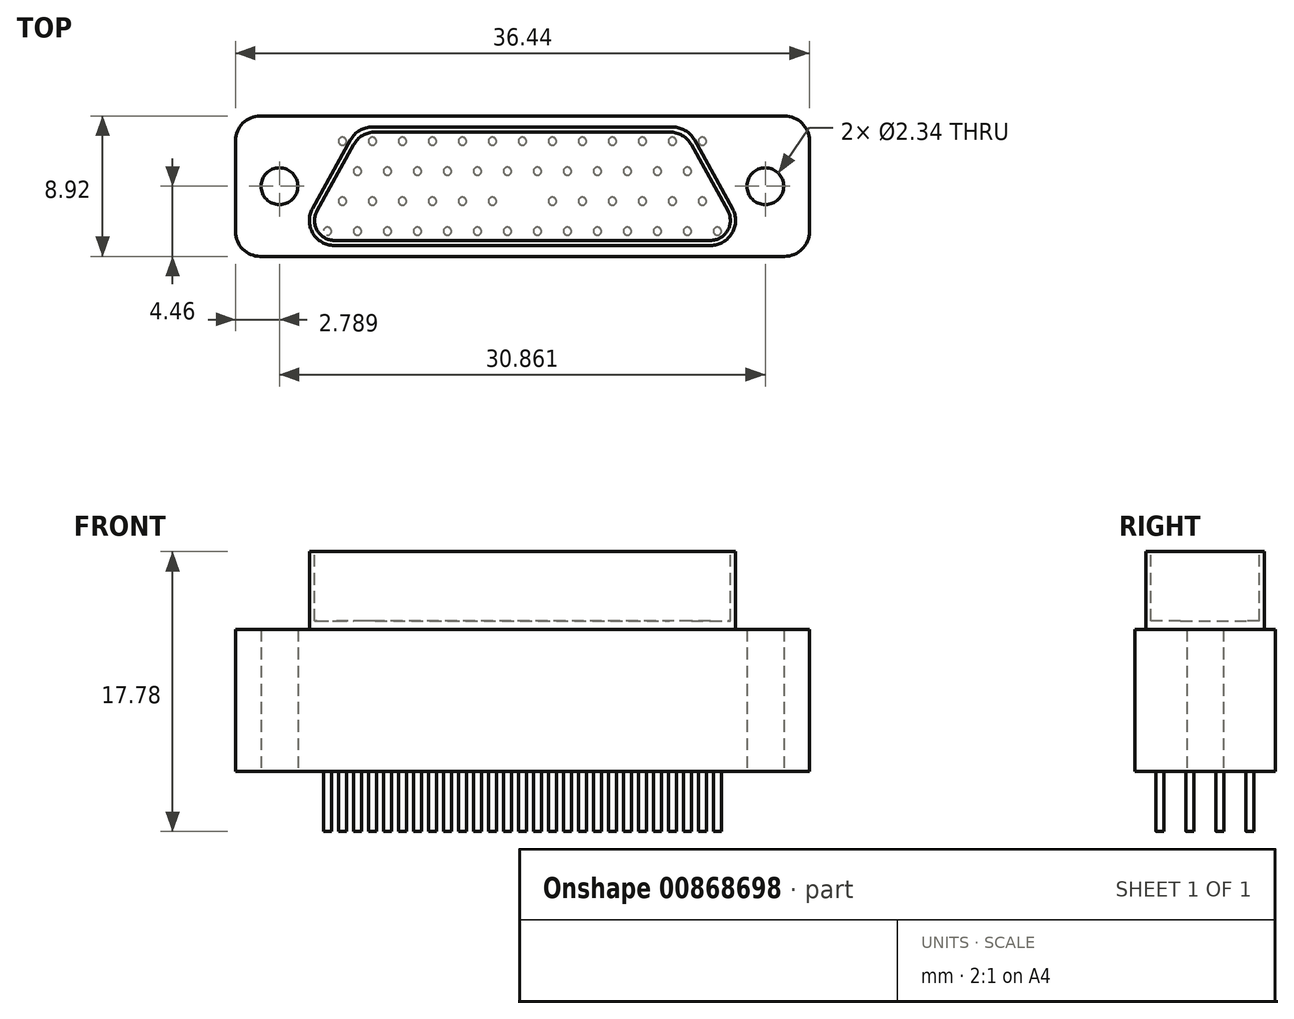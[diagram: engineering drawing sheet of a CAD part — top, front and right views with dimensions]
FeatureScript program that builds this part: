
annotation { "Feature Type Name" : "Feature", "Feature Type Description" : "" }
export const myFeature = defineFeature(function(context is Context, id is Id, definition is map)
    precondition{}
    {
        {
            var Q0;
            Q0=qCreatedBy(makeId("Top.planeOp"),FACE);
            var sketch = newSketch(context, id + "F0", { "sketchPlane" : qUnion([Q0])});
            skLineSegment(sketch, "E0.bottom", {"start": v(-16.65, 4.46) * mm, "end": v(16.65, 4.46) * mm});
            skLineSegment(sketch, "E0.top", {"start": v(-16.65, -4.46) * mm, "end": v(16.65, -4.46) * mm});
            skLineSegment(sketch, "E0.left", {"start": v(-18.22, 2.88) * mm, "end": v(-18.22, -2.88) * mm});
            skLineSegment(sketch, "E0.right", {"start": v(18.22, 2.88) * mm, "end": v(18.22, -2.88) * mm});
            skPoint(sketch, "E0.middle", {"position": v(0, 0) * mm});
            skCircle(sketch, "E1", {"center": v(-15.43, 0) * mm, "radius": 1.17 * mm});
            skCircle(sketch, "E2", {"center": v(15.43, 0) * mm, "radius": 1.17 * mm});
            skPoint(sketch, "E3.visualSharp", {"position": v(-18.22, -4.46) * mm});
            skArc(sketch, "E3.filletArc", {"start": v(-18.22, -2.88) * mm, "mid": v(-17.76, -4) * mm, "end": v(-16.65, -4.46) * mm});
            skPoint(sketch, "E4.visualSharp", {"position": v(-18.22, 4.46) * mm});
            skArc(sketch, "E4.filletArc", {"start": v(-16.65, 4.46) * mm, "mid": v(-17.76, 4) * mm, "end": v(-18.22, 2.88) * mm});
            skPoint(sketch, "E5.visualSharp", {"position": v(18.22, 4.46) * mm});
            skArc(sketch, "E5.filletArc", {"start": v(18.22, 2.88) * mm, "mid": v(17.76, 4) * mm, "end": v(16.65, 4.46) * mm});
            skPoint(sketch, "E6.visualSharp", {"position": v(18.22, -4.46) * mm});
            skArc(sketch, "E6.filletArc", {"start": v(16.65, -4.46) * mm, "mid": v(17.76, -4) * mm, "end": v(18.22, -2.88) * mm});
            skSolve(sketch);
        }
        {
            var Q0;
            Q0=makeQuery(id+"F0.imprint","IMPRINT",FACE,{"disambiguationData":[TD([[makeQuery(id+"F0.imprint","IMPRINT",EDGE,{"derivedFrom":sQuery(id+"F0.wireOp",EDGE,"E0.bottom")}),-1.0]])]});
            extrude(context, id + "F1", {"entities" : qUnion([Q0]), "endBound" : BoundingType.SYMMETRIC, "depth" : 9.02 * mm, "offsetDistance" : 25.4 * mm});
        }
        {
            var Q0;
            Q0=makeQuery(id+"F1.opExtrude","CAP_FACE",FACE,{"disambiguationData":[OSD([sQuery(id+"F0.wireOp",EDGE,"E0.bottom"),sQuery(id+"F0.wireOp",EDGE,"E0.top"),sQuery(id+"F0.wireOp",EDGE,"E0.left"),sQuery(id+"F0.wireOp",EDGE,"E0.right"),sQuery(id+"F0.wireOp",EDGE,"E1"),sQuery(id+"F0.wireOp",EDGE,"E2"),sQuery(id+"F0.wireOp",EDGE,"E3.filletArc"),sQuery(id+"F0.wireOp",EDGE,"E4.filletArc"),sQuery(id+"F0.wireOp",EDGE,"E5.filletArc"),sQuery(id+"F0.wireOp",EDGE,"E6.filletArc")])],"isStart":false});
            var sketch = newSketch(context, id + "F2", { "sketchPlane" : qUnion([Q0])});
            skPoint(sketch, "E7.middle", {"position": v(0, 0) * mm});
            skLineSegment(sketch, "E8.top", {"start": v(11.96, -3.76) * mm, "end": v(-11.96, -3.76) * mm});
            skLineSegment(sketch, "E9", {"start": v(-9.54, 3.76) * mm, "end": v(9.54, 3.76) * mm});
            skLineSegment(sketch, "E10", {"start": v(-13.33, -1.42) * mm, "end": v(-10.91, 2.95) * mm});
            skLineSegment(sketch, "E11", {"start": v(10.91, 2.95) * mm, "end": v(13.34, -1.42) * mm});
            skPoint(sketch, "E12.visualSharp", {"position": v(-10.46, 3.76) * mm});
            skArc(sketch, "E12.filletArc", {"start": v(-9.54, 3.76) * mm, "mid": v(-10.33, 3.54) * mm, "end": v(-10.91, 2.95) * mm});
            skPoint(sketch, "E13.visualSharp", {"position": v(-14.63, -3.76) * mm});
            skArc(sketch, "E13.filletArc", {"start": v(-13.33, -1.42) * mm, "mid": v(-13.31, -2.98) * mm, "end": v(-11.96, -3.76) * mm});
            skPoint(sketch, "E14.visualSharp", {"position": v(14.63, -3.76) * mm});
            skArc(sketch, "E14.filletArc", {"start": v(11.96, -3.76) * mm, "mid": v(13.32, -2.98) * mm, "end": v(13.34, -1.42) * mm});
            skPoint(sketch, "E15.visualSharp", {"position": v(10.46, 3.76) * mm});
            skArc(sketch, "E15.filletArc", {"start": v(10.91, 2.95) * mm, "mid": v(10.34, 3.54) * mm, "end": v(9.54, 3.76) * mm});
            skSolve(sketch);
        }
        {
            var Q0;
            Q0=qSketchRegion(id+"F2",true);
            extrude(context, id + "F3", {"entities" : qUnion([Q0]), "operationType" : NewBodyOperationType.ADD, "depth" : 4.95 * mm, "offsetDistance" : 25.4 * mm});
        }
        {
            var Q0;
            Q0=makeQuery(id+"F3.opExtrude","CAP_FACE",FACE,{"disambiguationData":[OSD([sQuery(id+"F2.wireOp",EDGE,"E8.top"),sQuery(id+"F2.wireOp",EDGE,"E9"),sQuery(id+"F2.wireOp",EDGE,"E10"),sQuery(id+"F2.wireOp",EDGE,"E11"),sQuery(id+"F2.wireOp",EDGE,"E12.filletArc"),sQuery(id+"F2.wireOp",EDGE,"E13.filletArc"),sQuery(id+"F2.wireOp",EDGE,"E14.filletArc"),sQuery(id+"F2.wireOp",EDGE,"E15.filletArc")])],"isStart":false});
            var sketch = newSketch(context, id + "F4", { "sketchPlane" : qUnion([Q0])});
            skLineSegment(sketch, "E16", {"start": v(-9.35, 3.44) * mm, "end": v(9.35, 3.44) * mm});
            skLineSegment(sketch, "E17", {"start": v(10.73, 2.63) * mm, "end": v(13.05, -1.56) * mm});
            skLineSegment(sketch, "E18", {"start": v(11.94, -3.44) * mm, "end": v(-11.94, -3.44) * mm});
            skLineSegment(sketch, "E19", {"start": v(-13.05, -1.56) * mm, "end": v(-10.73, 2.63) * mm});
            skPoint(sketch, "E20.visualSharp", {"position": v(-14.1, -3.44) * mm});
            skArc(sketch, "E20.filletArc", {"start": v(-13.05, -1.56) * mm, "mid": v(-13.03, -2.82) * mm, "end": v(-11.94, -3.44) * mm});
            skPoint(sketch, "E21.visualSharp", {"position": v(-10.28, 3.44) * mm});
            skArc(sketch, "E21.filletArc", {"start": v(-9.35, 3.44) * mm, "mid": v(-10.15, 3.22) * mm, "end": v(-10.73, 2.63) * mm});
            skPoint(sketch, "E22.visualSharp", {"position": v(10.28, 3.44) * mm});
            skArc(sketch, "E22.filletArc", {"start": v(10.73, 2.63) * mm, "mid": v(10.15, 3.22) * mm, "end": v(9.35, 3.44) * mm});
            skPoint(sketch, "E23.visualSharp", {"position": v(14.1, -3.44) * mm});
            skArc(sketch, "E23.filletArc", {"start": v(11.94, -3.44) * mm, "mid": v(13.03, -2.82) * mm, "end": v(13.05, -1.56) * mm});
            skSolve(sketch);
        }
        {
            var Q0;
            Q0=qSketchRegion(id+"F4",true);
            extrude(context, id + "F5", {"entities" : qUnion([Q0]), "operationType" : NewBodyOperationType.REMOVE, "depth" : -4.4 * mm, "offsetDistance" : 25.4 * mm});
        }
        {
            var Q0;
            Q0=makeQuery(id+"F1.opExtrude","CAP_FACE",FACE,{"disambiguationData":[OSD([sQuery(id+"F0.wireOp",EDGE,"E0.bottom"),sQuery(id+"F0.wireOp",EDGE,"E0.top"),sQuery(id+"F0.wireOp",EDGE,"E0.left"),sQuery(id+"F0.wireOp",EDGE,"E0.right"),sQuery(id+"F0.wireOp",EDGE,"E1"),sQuery(id+"F0.wireOp",EDGE,"E2"),sQuery(id+"F0.wireOp",EDGE,"E3.filletArc"),sQuery(id+"F0.wireOp",EDGE,"E4.filletArc"),sQuery(id+"F0.wireOp",EDGE,"E5.filletArc"),sQuery(id+"F0.wireOp",EDGE,"E6.filletArc")])],"isStart":true});
            var sketch = newSketch(context, id + "F6", { "sketchPlane" : qUnion([Q0])});
            skCircle(sketch, "E24", {"center": v(-12.38, 2.86) * mm, "radius": 0.25 * mm});
            skCircle(sketch, "E25.1.0.0", {"center": v(-10.48, 2.86) * mm, "radius": 0.25 * mm});
            skCircle(sketch, "E25.2.0.0", {"center": v(-8.57, 2.86) * mm, "radius": 0.25 * mm});
            skCircle(sketch, "E25.3.0.0", {"center": v(-6.67, 2.86) * mm, "radius": 0.25 * mm});
            skCircle(sketch, "E25.4.0.0", {"center": v(-4.76, 2.86) * mm, "radius": 0.25 * mm});
            skCircle(sketch, "E25.5.0.0", {"center": v(-2.86, 2.86) * mm, "radius": 0.25 * mm});
            skCircle(sketch, "E25.6.0.0", {"center": v(-0.95, 2.86) * mm, "radius": 0.25 * mm});
            skCircle(sketch, "E25.7.0.0", {"center": v(0.95, 2.86) * mm, "radius": 0.25 * mm});
            skCircle(sketch, "E25.8.0.0", {"center": v(2.86, 2.86) * mm, "radius": 0.25 * mm});
            skCircle(sketch, "E25.9.0.0", {"center": v(4.76, 2.86) * mm, "radius": 0.25 * mm});
            skCircle(sketch, "E25.10.0.0", {"center": v(6.67, 2.86) * mm, "radius": 0.25 * mm});
            skCircle(sketch, "E25.11.0.0", {"center": v(8.57, 2.86) * mm, "radius": 0.25 * mm});
            skCircle(sketch, "E25.12.0.0", {"center": v(10.48, 2.86) * mm, "radius": 0.25 * mm});
            skCircle(sketch, "E25.13.0.0", {"center": v(12.38, 2.86) * mm, "radius": 0.25 * mm});
            skLineSegment(sketch, "E25.direction1", {"start": v(-12.38, 2.86) * mm, "end": v(-10.48, 2.86) * mm, "construction": true});
            skCircle(sketch, "E26", {"center": v(-11.43, 0.95) * mm, "radius": 0.25 * mm});
            skCircle(sketch, "E27.1.0.0", {"center": v(-9.53, 0.95) * mm, "radius": 0.25 * mm});
            skCircle(sketch, "E27.2.0.0", {"center": v(-7.62, 0.95) * mm, "radius": 0.25 * mm});
            skCircle(sketch, "E27.3.0.0", {"center": v(-5.71, 0.95) * mm, "radius": 0.25 * mm});
            skCircle(sketch, "E27.4.0.0", {"center": v(-3.8, 0.95) * mm, "radius": 0.25 * mm});
            skCircle(sketch, "E27.5.0.0", {"center": v(-1.9, 0.95) * mm, "radius": 0.25 * mm});
            skLineSegment(sketch, "E27.direction1", {"start": v(-11.43, 0.95) * mm, "end": v(-9.53, 0.95) * mm, "construction": true});
            skCircle(sketch, "E28", {"center": v(-10.48, -0.95) * mm, "radius": 0.25 * mm});
            skCircle(sketch, "E29.1.0.0", {"center": v(-8.57, -0.95) * mm, "radius": 0.25 * mm});
            skCircle(sketch, "E29.2.0.0", {"center": v(-6.67, -0.95) * mm, "radius": 0.25 * mm});
            skCircle(sketch, "E29.3.0.0", {"center": v(-4.76, -0.95) * mm, "radius": 0.25 * mm});
            skCircle(sketch, "E29.4.0.0", {"center": v(-2.86, -0.95) * mm, "radius": 0.25 * mm});
            skCircle(sketch, "E29.5.0.0", {"center": v(-0.95, -0.95) * mm, "radius": 0.25 * mm});
            skLineSegment(sketch, "E29.direction1", {"start": v(-10.48, -0.95) * mm, "end": v(-8.57, -0.95) * mm, "construction": true});
            skLineSegment(sketch, "E30", {"start": v(0, 0.44) * mm, "end": v(0, -0.44) * mm});
            skLineSegment(sketch, "E31.MirrorCS", {"start": v(10.48, -0.95) * mm, "end": v(8.57, -0.95) * mm, "construction": true});
            skCircle(sketch, "E32.MirrorC", {"center": v(9.53, 0.95) * mm, "radius": 0.25 * mm});
            skCircle(sketch, "E33.MirrorC", {"center": v(7.62, 0.95) * mm, "radius": 0.25 * mm});
            skCircle(sketch, "E34.MirrorC", {"center": v(6.67, -0.95) * mm, "radius": 0.25 * mm});
            skCircle(sketch, "E35.MirrorC", {"center": v(11.43, 0.95) * mm, "radius": 0.25 * mm});
            skLineSegment(sketch, "E36.MirrorCS", {"start": v(11.43, 0.95) * mm, "end": v(9.53, 0.95) * mm, "construction": true});
            skCircle(sketch, "E37.MirrorC", {"center": v(4.76, -0.95) * mm, "radius": 0.25 * mm});
            skCircle(sketch, "E38.MirrorC", {"center": v(2.86, -0.95) * mm, "radius": 0.25 * mm});
            skCircle(sketch, "E39.MirrorC", {"center": v(5.71, 0.95) * mm, "radius": 0.25 * mm});
            skCircle(sketch, "E40.MirrorC", {"center": v(8.57, -0.95) * mm, "radius": 0.25 * mm});
            skCircle(sketch, "E41.MirrorC", {"center": v(1.9, 0.95) * mm, "radius": 0.25 * mm});
            skCircle(sketch, "E42.MirrorC", {"center": v(3.8, 0.95) * mm, "radius": 0.25 * mm});
            skCircle(sketch, "E43.MirrorC", {"center": v(10.48, -0.95) * mm, "radius": 0.25 * mm});
            skCircle(sketch, "E44.MirrorC", {"center": v(0.95, -0.95) * mm, "radius": 0.25 * mm});
            skCircle(sketch, "E45", {"center": v(-11.43, -2.86) * mm, "radius": 0.25 * mm});
            skCircle(sketch, "E46.1.0.0", {"center": v(-9.53, -2.86) * mm, "radius": 0.25 * mm});
            skCircle(sketch, "E46.2.0.0", {"center": v(-7.62, -2.86) * mm, "radius": 0.25 * mm});
            skCircle(sketch, "E46.3.0.0", {"center": v(-5.71, -2.86) * mm, "radius": 0.25 * mm});
            skCircle(sketch, "E46.4.0.0", {"center": v(-3.8, -2.86) * mm, "radius": 0.25 * mm});
            skCircle(sketch, "E46.5.0.0", {"center": v(-1.9, -2.86) * mm, "radius": 0.25 * mm});
            skCircle(sketch, "E46.6.0.0", {"center": v(0, -2.86) * mm, "radius": 0.25 * mm});
            skCircle(sketch, "E46.7.0.0", {"center": v(1.9, -2.86) * mm, "radius": 0.25 * mm});
            skCircle(sketch, "E46.8.0.0", {"center": v(3.81, -2.86) * mm, "radius": 0.25 * mm});
            skCircle(sketch, "E46.9.0.0", {"center": v(5.72, -2.86) * mm, "radius": 0.25 * mm});
            skCircle(sketch, "E46.10.0.0", {"center": v(7.62, -2.86) * mm, "radius": 0.25 * mm});
            skCircle(sketch, "E46.11.0.0", {"center": v(9.53, -2.86) * mm, "radius": 0.25 * mm});
            skCircle(sketch, "E46.12.0.0", {"center": v(11.43, -2.86) * mm, "radius": 0.25 * mm});
            skLineSegment(sketch, "E46.direction1", {"start": v(-11.43, -2.86) * mm, "end": v(-9.53, -2.86) * mm, "construction": true});
            skSolve(sketch);
        }
        {
            var Q0;
            Q0 = qSketchRegion(id + "F6", true);
            extrude(context, id + "F7", {"entities" : qUnion([Q0]), "operationType" : NewBodyOperationType.ADD, "depth" : 3.8 * mm, "offsetDistance" : 25.4 * mm});
        }
    });
